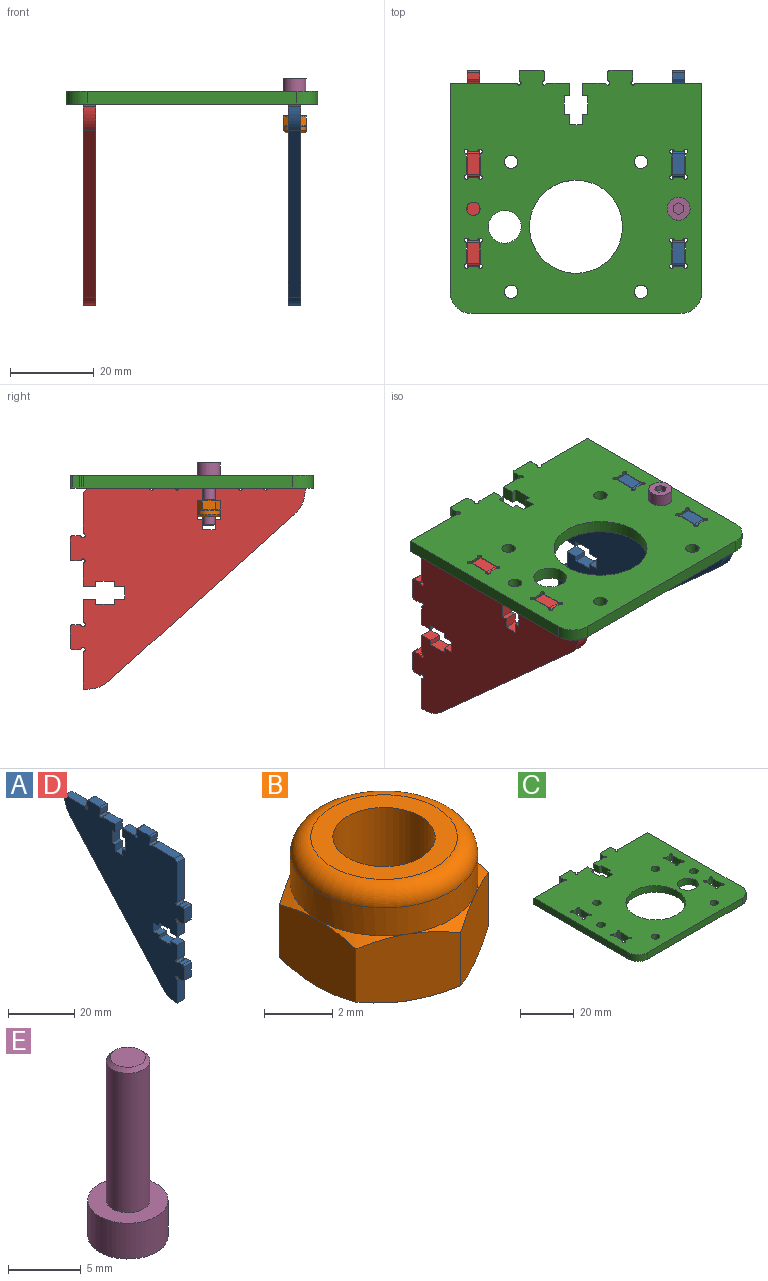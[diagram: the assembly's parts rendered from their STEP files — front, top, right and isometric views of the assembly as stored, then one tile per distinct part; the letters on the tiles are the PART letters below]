
ASSEMBLY  parts=5 mates=4
PART A: 82 faces, bbox 3x51x56 mm
  f0: plane 14.53x3mm, normal (0,-1,0), area 43.6mm2, adj f19,f20,f21,f80
  f1: plane 3x1.63mm, normal (0,0,1), area 4.9mm2, adj f19,f20,f67,f81
  f2: plane 5.18x3mm, normal (0,-1,0), area 15.6mm2, adj f19,f20,f53,f77
  f3: plane 3x1.63mm, normal (0,0,-1), area 4.9mm2, adj f19,f20,f66,f78
  f4: plane 8.53x3mm, normal (0,-1,0), area 25.6mm2, adj f17,f19,f20,f74
  f5: plane 3x1.63mm, normal (0,0,-1), area 4.9mm2, adj f19,f20,f69,f75
  f6: plane 5.18x3mm, normal (0,-1,0), area 15.6mm2, adj f19,f20,f54,f71
  f7: plane 3x1.63mm, normal (0,0,1), area 4.9mm2, adj f19,f20,f68,f72
  f8: plane 8.53x3mm, normal (0,0,1), area 25.6mm2, adj f16,f19,f20,f51
  f9: plane 3x1.63mm, normal (0,1,0), area 4.9mm2, adj f19,f20,f38,f52
  f10: plane 5.18x3mm, normal (0,0,1), area 15.6mm2, adj f19,f20,f24,f48
  f11: plane 3x1.63mm, normal (0,-1,0), area 4.9mm2, adj f19,f20,f37,f49
  f12: plane 9.53x3mm, normal (0,0,1), area 28.6mm2, adj f19,f20,f21,f45
  f13: plane 3x1.63mm, normal (0,-1,0), area 4.9mm2, adj f19,f20,f40,f46
  f14: plane 5.18x3mm, normal (0,0,1), area 15.6mm2, adj f19,f20,f25,f42
  f15: plane 3x1.63mm, normal (0,1,0), area 4.9mm2, adj f19,f20,f39,f43
  f16: plane 3x1.13mm, normal (0,1,0), area 3.4mm2, adj f8,f19,f20,f23
  f17: plane 3x0.65mm, normal (0,0,-1), area 2mm2, adj f4,f19,f20,f22
  f18: plane 44.37x39.85mm, normal (0,0.74,-0.67), area 178.9mm2, adj f19,f20,f22,f23
  f19: plane 56x51mm, normal (1,0,0), area 1445.5mm2, adj f0,f1,f2,f3,f4,f5,f6,f7
  f20: plane 56x51mm, normal (-1,0,0), area 1445.5mm2, adj f0,f1,f2,f3,f4,f5,f6,f7
  f21: plane 3x1mm, normal (0,-0.71,0.71), area 4.2mm2, adj f0,f12,f19,f20
  f22: cylinder r=7.5mm len=5.58mm, axis (-1,0,0), area 18.9mm2, adj f17,f18,f19,f20
  f23: cylinder r=7.5mm len=5.01mm, axis (-1,0,0), area 16.5mm2, adj f16,f18,f19,f20
  f24: plane 3x3mm, normal (0,-1,0), area 9mm2, adj f10,f19,f20,f34
  f25: plane 3x3mm, normal (0,1,0), area 9mm2, adj f14,f19,f20,f26
  f26: plane 3x1.23mm, normal (0,0,-1), area 3.7mm2, adj f19,f20,f25,f27
  f27: plane 4.5x3mm, normal (0,1,0), area 13.5mm2, adj f19,f20,f26,f28
  f28: plane 3x1.23mm, normal (0,0,1), area 3.7mm2, adj f19,f20,f27,f29
  f29: plane 3x2.5mm, normal (0,1,0), area 7.5mm2, adj f19,f20,f28,f30
  f30: plane 3.1x3mm, normal (0,0,1), area 9.3mm2, adj f19,f20,f29,f31
  f31: plane 3x2.5mm, normal (0,-1,0), area 7.5mm2, adj f19,f20,f30,f32
  f32: plane 3x1.23mm, normal (0,0,1), area 3.7mm2, adj f19,f20,f31,f33
  f33: plane 4.5x3mm, normal (0,-1,0), area 13.5mm2, adj f19,f20,f32,f34
  f34: plane 3x1.23mm, normal (0,0,-1), area 3.7mm2, adj f19,f20,f24,f33
  f35: plane 5x3mm, normal (0,0,1), area 15mm2, adj f19,f20,f39,f40
  f36: plane 5x3mm, normal (0,0,1), area 15mm2, adj f19,f20,f37,f38
  f37: cylinder r=0.5mm len=3mm, axis (-1,0,0), area 2.4mm2, adj f11,f19,f20,f36
  f38: cylinder r=0.5mm len=3mm, axis (-1,0,0), area 2.4mm2, adj f9,f19,f20,f36
  f39: cylinder r=0.5mm len=3mm, axis (-1,0,0), area 2.4mm2, adj f15,f19,f20,f35
  f40: cylinder r=0.5mm len=3mm, axis (-1,0,0), area 2.4mm2, adj f13,f19,f20,f35
  f41: cylinder r=0.5mm len=3mm, axis (1,0,0), area 5.5mm2, adj f19,f20,f42,f43
  f42: cylinder r=0.5mm len=3mm, axis (1,0,0), area 1.6mm2, adj f14,f19,f20,f41
  f43: cylinder r=0.5mm len=3mm, axis (1,0,0), area 1.6mm2, adj f15,f19,f20,f41
  f44: cylinder r=0.5mm len=3mm, axis (1,0,0), area 5.5mm2, adj f19,f20,f45,f46
  f45: cylinder r=0.5mm len=3mm, axis (1,0,0), area 1.6mm2, adj f12,f19,f20,f44
  f46: cylinder r=0.5mm len=3mm, axis (1,0,0), area 1.6mm2, adj f13,f19,f20,f44
  f47: cylinder r=0.5mm len=3mm, axis (1,0,0), area 5.5mm2, adj f19,f20,f48,f49
  f48: cylinder r=0.5mm len=3mm, axis (1,0,0), area 1.6mm2, adj f10,f19,f20,f47
  f49: cylinder r=0.5mm len=3mm, axis (1,0,0), area 1.6mm2, adj f11,f19,f20,f47
  f50: cylinder r=0.5mm len=3mm, axis (1,0,0), area 5.5mm2, adj f19,f20,f51,f52
  f51: cylinder r=0.5mm len=3mm, axis (1,0,0), area 1.6mm2, adj f8,f19,f20,f50
  f52: cylinder r=0.5mm len=3mm, axis (1,0,0), area 1.6mm2, adj f9,f19,f20,f50
  f53: plane 3x3mm, normal (0,0,-1), area 9mm2, adj f2,f19,f20,f63
  f54: plane 3x3mm, normal (0,0,1), area 9mm2, adj f6,f19,f20,f55
  f55: plane 3x1.23mm, normal (0,1,0), area 3.7mm2, adj f19,f20,f54,f56
  f56: plane 4.5x3mm, normal (0,0,1), area 13.5mm2, adj f19,f20,f55,f57
  f57: plane 3x1.23mm, normal (0,-1,0), area 3.7mm2, adj f19,f20,f56,f58
  f58: plane 3x2.5mm, normal (0,0,1), area 7.5mm2, adj f19,f20,f57,f59
  f59: plane 3.1x3mm, normal (0,-1,0), area 9.3mm2, adj f19,f20,f58,f60
  f60: plane 3x2.5mm, normal (0,0,-1), area 7.5mm2, adj f19,f20,f59,f61
  f61: plane 3x1.23mm, normal (0,-1,0), area 3.7mm2, adj f19,f20,f60,f62
  f62: plane 4.5x3mm, normal (0,0,-1), area 13.5mm2, adj f19,f20,f61,f63
  f63: plane 3x1.23mm, normal (0,1,0), area 3.7mm2, adj f19,f20,f53,f62
  f64: plane 5x3mm, normal (0,-1,0), area 15mm2, adj f19,f20,f68,f69
  f65: plane 5x3mm, normal (0,-1,0), area 15mm2, adj f19,f20,f66,f67
  f66: cylinder r=0.5mm len=3mm, axis (-1,0,0), area 2.4mm2, adj f3,f19,f20,f65
  f67: cylinder r=0.5mm len=3mm, axis (-1,0,0), area 2.4mm2, adj f1,f19,f20,f65
  f68: cylinder r=0.5mm len=3mm, axis (-1,0,0), area 2.4mm2, adj f7,f19,f20,f64
  f69: cylinder r=0.5mm len=3mm, axis (-1,0,0), area 2.4mm2, adj f5,f19,f20,f64
  f70: cylinder r=0.5mm len=3mm, axis (1,0,0), area 5.5mm2, adj f19,f20,f71,f72
  f71: cylinder r=0.5mm len=3mm, axis (1,0,0), area 1.6mm2, adj f6,f19,f20,f70
  f72: cylinder r=0.5mm len=3mm, axis (1,0,0), area 1.6mm2, adj f7,f19,f20,f70
  f73: cylinder r=0.5mm len=3mm, axis (1,0,0), area 5.5mm2, adj f19,f20,f74,f75
  f74: cylinder r=0.5mm len=3mm, axis (1,0,0), area 1.6mm2, adj f4,f19,f20,f73
  f75: cylinder r=0.5mm len=3mm, axis (1,0,0), area 1.6mm2, adj f5,f19,f20,f73
  f76: cylinder r=0.5mm len=3mm, axis (1,0,0), area 5.5mm2, adj f19,f20,f77,f78
  f77: cylinder r=0.5mm len=3mm, axis (1,0,0), area 1.6mm2, adj f2,f19,f20,f76
  f78: cylinder r=0.5mm len=3mm, axis (1,0,0), area 1.6mm2, adj f3,f19,f20,f76
  f79: cylinder r=0.5mm len=3mm, axis (1,0,0), area 5.5mm2, adj f19,f20,f80,f81
  f80: cylinder r=0.5mm len=3mm, axis (1,0,0), area 1.6mm2, adj f0,f19,f20,f79
  f81: cylinder r=0.5mm len=3mm, axis (1,0,0), area 1.6mm2, adj f1,f19,f20,f79
PART B: 23 faces, bbox 6.6x6.6x4.3 mm
  f0: plane 5.5x5.5mm, normal (0,0,-1), area 16.7mm2, adj f3,f6,f7,f9,f11,f13,f15
  f1: cylinder r=2.75mm len=5.5mm, axis (0,0,-1), area 17.3mm2, adj f4,f5,f8,f10,f12,f14,f22
  f2: plane 4.3x4.3mm, normal (0,0,1), area 7.5mm2, adj f3,f22
  f3: cylinder r=1.5mm len=4mm, axis (0,0,-1), area 37.7mm2, adj f0,f2
  f4: cone r=3.18mm half-angle=60deg, axis (0,0,-1), area 0.7mm2, adj f1,f16,f21
  f5: cone r=3.18mm half-angle=60deg, axis (0,0,-1), area 0.7mm2, adj f1,f16,f17
  f6: cone r=3.18mm half-angle=60deg, axis (0,0,1), area 0.7mm2, adj f0,f16,f21
  f7: cone r=3.18mm half-angle=60deg, axis (0,0,1), area 0.7mm2, adj f0,f16,f17
  f8: cone r=3.18mm half-angle=60deg, axis (0,0,-1), area 0.7mm2, adj f1,f17,f18
  f9: cone r=3.18mm half-angle=60deg, axis (0,0,1), area 0.7mm2, adj f0,f17,f18
  f10: cone r=3.18mm half-angle=60deg, axis (0,0,-1), area 0.7mm2, adj f1,f18,f19
  f11: cone r=3.18mm half-angle=60deg, axis (0,0,1), area 0.7mm2, adj f0,f18,f19
  f12: cone r=3.18mm half-angle=60deg, axis (0,0,-1), area 0.7mm2, adj f1,f19,f20
  f13: cone r=3.18mm half-angle=60deg, axis (0,0,1), area 0.7mm2, adj f0,f19,f20
  f14: cone r=3.18mm half-angle=60deg, axis (0,0,-1), area 0.7mm2, adj f1,f20,f21
  f15: cone r=3.18mm half-angle=60deg, axis (0,0,1), area 0.7mm2, adj f0,f20,f21
  f16: plane 3.01x2.67mm, normal (0.5,-0.87,0), area 7.1mm2, adj f4,f5,f6,f7,f17,f21
  f17: plane 3.01x2.67mm, normal (-0.5,-0.87,0), area 7.1mm2, adj f5,f7,f8,f9,f16,f18
  f18: plane 3.44x2.66mm, normal (-1,0,0), area 7.1mm2, adj f8,f9,f10,f11,f17,f19
  f19: plane 3.01x2.67mm, normal (-0.5,0.87,0), area 7.1mm2, adj f10,f11,f12,f13,f18,f20
  f20: plane 3.01x2.67mm, normal (0.5,0.87,0), area 7.1mm2, adj f12,f13,f14,f15,f19,f21
  f21: plane 3.44x2.66mm, normal (1,0,0), area 7.1mm2, adj f4,f6,f14,f15,f16,f20
  f22: torus R=2.15mm, axis (0,0,1), area 15mm2, adj f1,f2
PART C: 116 faces, bbox 60x58x3 mm
  f0: plane 4.47x3mm, normal (1,0,0), area 13.4mm2, adj f8,f9,f112,f114
  f1: plane 3x1.57mm, normal (0,-1,0), area 4.7mm2, adj f8,f9,f105,f115
  f2: plane 3x1.57mm, normal (0,1,0), area 4.7mm2, adj f8,f9,f109,f111
  f3: plane 4.47x3mm, normal (-1,0,0), area 13.4mm2, adj f8,f9,f106,f108
  f4: plane 4.47x3mm, normal (1,0,0), area 13.4mm2, adj f8,f9,f100,f102
  f5: plane 3x1.57mm, normal (0,1,0), area 4.7mm2, adj f8,f9,f93,f103
  f6: plane 3x1.57mm, normal (0,-1,0), area 4.7mm2, adj f8,f9,f97,f99
  f7: plane 4.47x3mm, normal (-1,0,0), area 13.4mm2, adj f8,f9,f94,f96
  f8: plane 60x58mm, normal (0,0,1), area 2705.5mm2, adj f0,f1,f2,f3,f4,f5,f6,f7
  f9: plane 60x58mm, normal (0,0,-1), area 2705.5mm2, adj f0,f1,f2,f3,f4,f5,f6,f7
  f10: plane 4.47x3mm, normal (1,0,0), area 13.4mm2, adj f8,f9,f87,f89
  f11: plane 3x1.57mm, normal (0,-1,0), area 4.7mm2, adj f8,f9,f80,f90
  f12: plane 3x1.57mm, normal (0,1,0), area 4.7mm2, adj f8,f9,f84,f86
  f13: plane 4.47x3mm, normal (-1,0,0), area 13.4mm2, adj f8,f9,f81,f83
  f14: plane 4.47x3mm, normal (1,0,0), area 13.4mm2, adj f8,f9,f75,f77
  f15: plane 3x1.57mm, normal (0,1,0), area 4.7mm2, adj f8,f9,f68,f78
  f16: plane 3x1.57mm, normal (0,-1,0), area 4.7mm2, adj f8,f9,f72,f74
  f17: plane 4.47x3mm, normal (-1,0,0), area 13.4mm2, adj f8,f9,f69,f71
  f18: plane 15.53x3mm, normal (0,1,0), area 46.6mm2, adj f8,f9,f26,f64
  f19: plane 3x1.63mm, normal (1,0,0), area 4.9mm2, adj f8,f9,f51,f65
  f20: plane 5.18x3mm, normal (0,1,0), area 15.6mm2, adj f8,f9,f37,f61
  f21: plane 3x1.63mm, normal (-1,0,0), area 4.9mm2, adj f8,f9,f50,f62
  f22: plane 15.53x3mm, normal (0,1,0), area 46.6mm2, adj f8,f9,f27,f58
  f23: plane 3x1.63mm, normal (-1,0,0), area 4.9mm2, adj f8,f9,f53,f59
  f24: plane 5.18x3mm, normal (0,1,0), area 15.6mm2, adj f8,f9,f38,f55
  f25: plane 3x1.63mm, normal (1,0,0), area 4.9mm2, adj f8,f9,f52,f56
  f26: plane 50x3mm, normal (1,0,0), area 150mm2, adj f8,f9,f18,f36
  f27: plane 50x3mm, normal (-1,0,0), area 150mm2, adj f8,f9,f22,f35
  f28: cylinder r=1.6mm len=3.2mm, axis (0,0,-1), area 30.2mm2, adj f8,f9
  f29: cylinder r=1.6mm len=3.2mm, axis (0,0,-1), area 30.2mm2, adj f8,f9
  f30: plane 50x3mm, normal (0,-1,0), area 150mm2, adj f8,f9,f35,f36
  f31: cylinder r=11.1mm len=22.2mm, axis (0,0,-1), area 209.2mm2, adj f8,f9
  f32: cylinder r=1.6mm len=3.2mm, axis (0,0,-1), area 30.2mm2, adj f8,f9
  f33: cylinder r=1.6mm len=3.2mm, axis (0,0,-1), area 30.2mm2, adj f8,f9
  f34: cylinder r=3.9mm len=7.8mm, axis (0,0,-1), area 73.5mm2, adj f8,f9
  f35: cylinder r=5mm len=5mm, axis (0,0,-1), area 23.6mm2, adj f8,f9,f27,f30
  f36: cylinder r=5mm len=5mm, axis (0,0,-1), area 23.6mm2, adj f8,f9,f26,f30
  f37: plane 3x3mm, normal (-1,0,0), area 9mm2, adj f8,f9,f20,f47
  f38: plane 3x3mm, normal (1,0,0), area 9mm2, adj f8,f9,f24,f39
  f39: plane 3x1.23mm, normal (0,-1,0), area 3.7mm2, adj f8,f9,f38,f40
  f40: plane 4.5x3mm, normal (1,0,0), area 13.5mm2, adj f8,f9,f39,f41
  f41: plane 3x1.23mm, normal (0,1,0), area 3.7mm2, adj f8,f9,f40,f42
  f42: plane 3x2.5mm, normal (1,0,0), area 7.5mm2, adj f8,f9,f41,f43
  f43: plane 3.1x3mm, normal (0,1,0), area 9.3mm2, adj f8,f9,f42,f44
  f44: plane 3x2.5mm, normal (-1,0,0), area 7.5mm2, adj f8,f9,f43,f45
  f45: plane 3x1.23mm, normal (0,1,0), area 3.7mm2, adj f8,f9,f44,f46
  f46: plane 4.5x3mm, normal (-1,0,0), area 13.5mm2, adj f8,f9,f45,f47
  f47: plane 3x1.23mm, normal (0,-1,0), area 3.7mm2, adj f8,f9,f37,f46
  f48: plane 5x3mm, normal (0,1,0), area 15mm2, adj f8,f9,f52,f53
  f49: plane 5x3mm, normal (0,1,0), area 15mm2, adj f8,f9,f50,f51
  f50: cylinder r=0.5mm len=3mm, axis (0,0,-1), area 2.4mm2, adj f8,f9,f21,f49
  f51: cylinder r=0.5mm len=3mm, axis (0,0,-1), area 2.4mm2, adj f8,f9,f19,f49
  f52: cylinder r=0.5mm len=3mm, axis (0,0,-1), area 2.4mm2, adj f8,f9,f25,f48
  f53: cylinder r=0.5mm len=3mm, axis (0,0,-1), area 2.4mm2, adj f8,f9,f23,f48
  f54: cylinder r=0.5mm len=3mm, axis (0,0,1), area 5.5mm2, adj f8,f9,f55,f56
  f55: cylinder r=0.5mm len=3mm, axis (0,0,1), area 1.6mm2, adj f8,f9,f24,f54
  f56: cylinder r=0.5mm len=3mm, axis (0,0,1), area 1.6mm2, adj f8,f9,f25,f54
  f57: cylinder r=0.5mm len=3mm, axis (0,0,1), area 5.5mm2, adj f8,f9,f58,f59
  f58: cylinder r=0.5mm len=3mm, axis (0,0,1), area 1.6mm2, adj f8,f9,f22,f57
  f59: cylinder r=0.5mm len=3mm, axis (0,0,1), area 1.6mm2, adj f8,f9,f23,f57
  f60: cylinder r=0.5mm len=3mm, axis (0,0,1), area 5.5mm2, adj f8,f9,f61,f62
  f61: cylinder r=0.5mm len=3mm, axis (0,0,1), area 1.6mm2, adj f8,f9,f20,f60
  f62: cylinder r=0.5mm len=3mm, axis (0,0,1), area 1.6mm2, adj f8,f9,f21,f60
  f63: cylinder r=0.5mm len=3mm, axis (0,0,1), area 5.5mm2, adj f8,f9,f64,f65
  f64: cylinder r=0.5mm len=3mm, axis (0,0,1), area 1.6mm2, adj f8,f9,f18,f63
  f65: cylinder r=0.5mm len=3mm, axis (0,0,1), area 1.6mm2, adj f8,f9,f19,f63
  f66: cylinder r=1.6mm len=3.2mm, axis (0,0,-1), area 30.2mm2, adj f8,f9
  f67: cylinder r=0.5mm len=3mm, axis (0,0,1), area 5.5mm2, adj f8,f9,f68,f69
  f68: cylinder r=0.5mm len=3mm, axis (0,0,1), area 1.6mm2, adj f8,f9,f15,f67
  f69: cylinder r=0.5mm len=3mm, axis (0,0,1), area 1.6mm2, adj f8,f9,f17,f67
  f70: cylinder r=0.5mm len=3mm, axis (0,0,1), area 5.5mm2, adj f8,f9,f71,f72
  f71: cylinder r=0.5mm len=3mm, axis (0,0,1), area 1.6mm2, adj f8,f9,f17,f70
  f72: cylinder r=0.5mm len=3mm, axis (0,0,1), area 1.6mm2, adj f8,f9,f16,f70
  f73: cylinder r=0.5mm len=3mm, axis (0,0,1), area 5.5mm2, adj f8,f9,f74,f75
  f74: cylinder r=0.5mm len=3mm, axis (0,0,1), area 1.6mm2, adj f8,f9,f16,f73
  f75: cylinder r=0.5mm len=3mm, axis (0,0,1), area 1.6mm2, adj f8,f9,f14,f73
  f76: cylinder r=0.5mm len=3mm, axis (0,0,1), area 5.5mm2, adj f8,f9,f77,f78
  f77: cylinder r=0.5mm len=3mm, axis (0,0,1), area 1.6mm2, adj f8,f9,f14,f76
  f78: cylinder r=0.5mm len=3mm, axis (0,0,1), area 1.6mm2, adj f8,f9,f15,f76
  f79: cylinder r=0.5mm len=3mm, axis (0,0,1), area 5.5mm2, adj f8,f9,f80,f81
  f80: cylinder r=0.5mm len=3mm, axis (0,0,1), area 1.6mm2, adj f8,f9,f11,f79
  f81: cylinder r=0.5mm len=3mm, axis (0,0,1), area 1.6mm2, adj f8,f9,f13,f79
  f82: cylinder r=0.5mm len=3mm, axis (0,0,1), area 5.5mm2, adj f8,f9,f83,f84
  f83: cylinder r=0.5mm len=3mm, axis (0,0,1), area 1.6mm2, adj f8,f9,f13,f82
  f84: cylinder r=0.5mm len=3mm, axis (0,0,1), area 1.6mm2, adj f8,f9,f12,f82
  f85: cylinder r=0.5mm len=3mm, axis (0,0,1), area 5.5mm2, adj f8,f9,f86,f87
  f86: cylinder r=0.5mm len=3mm, axis (0,0,1), area 1.6mm2, adj f8,f9,f12,f85
  f87: cylinder r=0.5mm len=3mm, axis (0,0,1), area 1.6mm2, adj f8,f9,f10,f85
  f88: cylinder r=0.5mm len=3mm, axis (0,0,1), area 5.5mm2, adj f8,f9,f89,f90
  f89: cylinder r=0.5mm len=3mm, axis (0,0,1), area 1.6mm2, adj f8,f9,f10,f88
  f90: cylinder r=0.5mm len=3mm, axis (0,0,1), area 1.6mm2, adj f8,f9,f11,f88
  f91: cylinder r=1.6mm len=3.2mm, axis (0,0,-1), area 30.2mm2, adj f8,f9
  f92: cylinder r=0.5mm len=3mm, axis (0,0,1), area 5.5mm2, adj f8,f9,f93,f94
  f93: cylinder r=0.5mm len=3mm, axis (0,0,1), area 1.6mm2, adj f5,f8,f9,f92
  f94: cylinder r=0.5mm len=3mm, axis (0,0,1), area 1.6mm2, adj f7,f8,f9,f92
  f95: cylinder r=0.5mm len=3mm, axis (0,0,1), area 5.5mm2, adj f8,f9,f96,f97
  f96: cylinder r=0.5mm len=3mm, axis (0,0,1), area 1.6mm2, adj f7,f8,f9,f95
  f97: cylinder r=0.5mm len=3mm, axis (0,0,1), area 1.6mm2, adj f6,f8,f9,f95
  f98: cylinder r=0.5mm len=3mm, axis (0,0,1), area 5.5mm2, adj f8,f9,f99,f100
  f99: cylinder r=0.5mm len=3mm, axis (0,0,1), area 1.6mm2, adj f6,f8,f9,f98
  f100: cylinder r=0.5mm len=3mm, axis (0,0,1), area 1.6mm2, adj f4,f8,f9,f98
  f101: cylinder r=0.5mm len=3mm, axis (0,0,1), area 5.5mm2, adj f8,f9,f102,f103
  f102: cylinder r=0.5mm len=3mm, axis (0,0,1), area 1.6mm2, adj f4,f8,f9,f101
  f103: cylinder r=0.5mm len=3mm, axis (0,0,1), area 1.6mm2, adj f5,f8,f9,f101
  f104: cylinder r=0.5mm len=3mm, axis (0,0,1), area 5.5mm2, adj f8,f9,f105,f106
  f105: cylinder r=0.5mm len=3mm, axis (0,0,1), area 1.6mm2, adj f1,f8,f9,f104
  f106: cylinder r=0.5mm len=3mm, axis (0,0,1), area 1.6mm2, adj f3,f8,f9,f104
  f107: cylinder r=0.5mm len=3mm, axis (0,0,1), area 5.5mm2, adj f8,f9,f108,f109
  f108: cylinder r=0.5mm len=3mm, axis (0,0,1), area 1.6mm2, adj f3,f8,f9,f107
  f109: cylinder r=0.5mm len=3mm, axis (0,0,1), area 1.6mm2, adj f2,f8,f9,f107
  f110: cylinder r=0.5mm len=3mm, axis (0,0,1), area 5.5mm2, adj f8,f9,f111,f112
  f111: cylinder r=0.5mm len=3mm, axis (0,0,1), area 1.6mm2, adj f2,f8,f9,f110
  f112: cylinder r=0.5mm len=3mm, axis (0,0,1), area 1.6mm2, adj f0,f8,f9,f110
  f113: cylinder r=0.5mm len=3mm, axis (0,0,1), area 5.5mm2, adj f8,f9,f114,f115
  f114: cylinder r=0.5mm len=3mm, axis (0,0,1), area 1.6mm2, adj f0,f8,f9,f113
  f115: cylinder r=0.5mm len=3mm, axis (0,0,1), area 1.6mm2, adj f1,f8,f9,f113
PART D: same geometry as A
PART E: 13 faces, bbox 5.5x5.5x15 mm
  f0: plane 5.5x5.5mm, normal (0,0,-1), area 18.3mm2, adj f2,f6,f7,f8,f9,f10,f11
  f1: plane 2.4x2.4mm, normal (0,0,1), area 4.5mm2, adj f5
  f2: cylinder r=2.75mm len=5.5mm, axis (0,0,-1), area 51.8mm2, adj f0,f3
  f3: plane 5.5x5.5mm, normal (0,0,1), area 16.7mm2, adj f2,f4
  f4: cylinder r=1.5mm len=11.7mm, axis (0,0,-1), area 110.3mm2, adj f3,f5
  f5: cone r=1.5mm half-angle=45deg, axis (0,0,-1), area 3.6mm2, adj f1,f4
  f6: plane 1.44x1.3mm, normal (-1,0,0), area 1.9mm2, adj f0,f7,f11,f12
  f7: plane 1.3x1.25mm, normal (-0.5,-0.87,0), area 1.9mm2, adj f0,f6,f8,f12
  f8: plane 1.3x1.25mm, normal (0.5,-0.87,0), area 1.9mm2, adj f0,f7,f9,f12
  f9: plane 1.44x1.3mm, normal (1,0,0), area 1.9mm2, adj f0,f8,f10,f12
  f10: plane 1.3x1.25mm, normal (0.5,0.87,0), area 1.9mm2, adj f0,f9,f11,f12
  f11: plane 1.3x1.25mm, normal (-0.5,0.87,0), area 1.9mm2, adj f0,f6,f10,f12
  f12: plane 2.89x2.5mm, normal (0,0,-1), area 5.4mm2, adj f6,f7,f8,f9,f10,f11
PLACE A rot(axis=(-1,0,0),90deg) t=(-223.75,-19.79,-54.71)mm
PLACE B rot(axis=(1,0,0),180deg) t=(-242.25,-27.81,-119.39)mm
PLACE C rot(axis=(0,-1,0),180deg) t=(-246.75,-32.11,-113.54)mm
PLACE D rot(axis=(-1,0,0),90deg) t=(-272.75,-19.79,-54.71)mm
PLACE E rot(axis=(1,0,0),180deg) t=(-262.25,-27.81,-110.54)mm
MATE fastened B.f1 <-> E.f2  axis (0,0,1) through (-222.25,-27.81,-119.39)mm
MATE fastened A.f6 <-> C.f91  axis (0,0,1) through (-222.25,-27.81,-116.54)mm
MATE fastened D.f6 <-> C.f66  axis (0,0,1) through (-271.25,-27.81,-116.54)mm
MATE fastened E.f2 <-> C.f91  axis (0,0,-1) through (-222.25,-27.81,-113.54)mm
